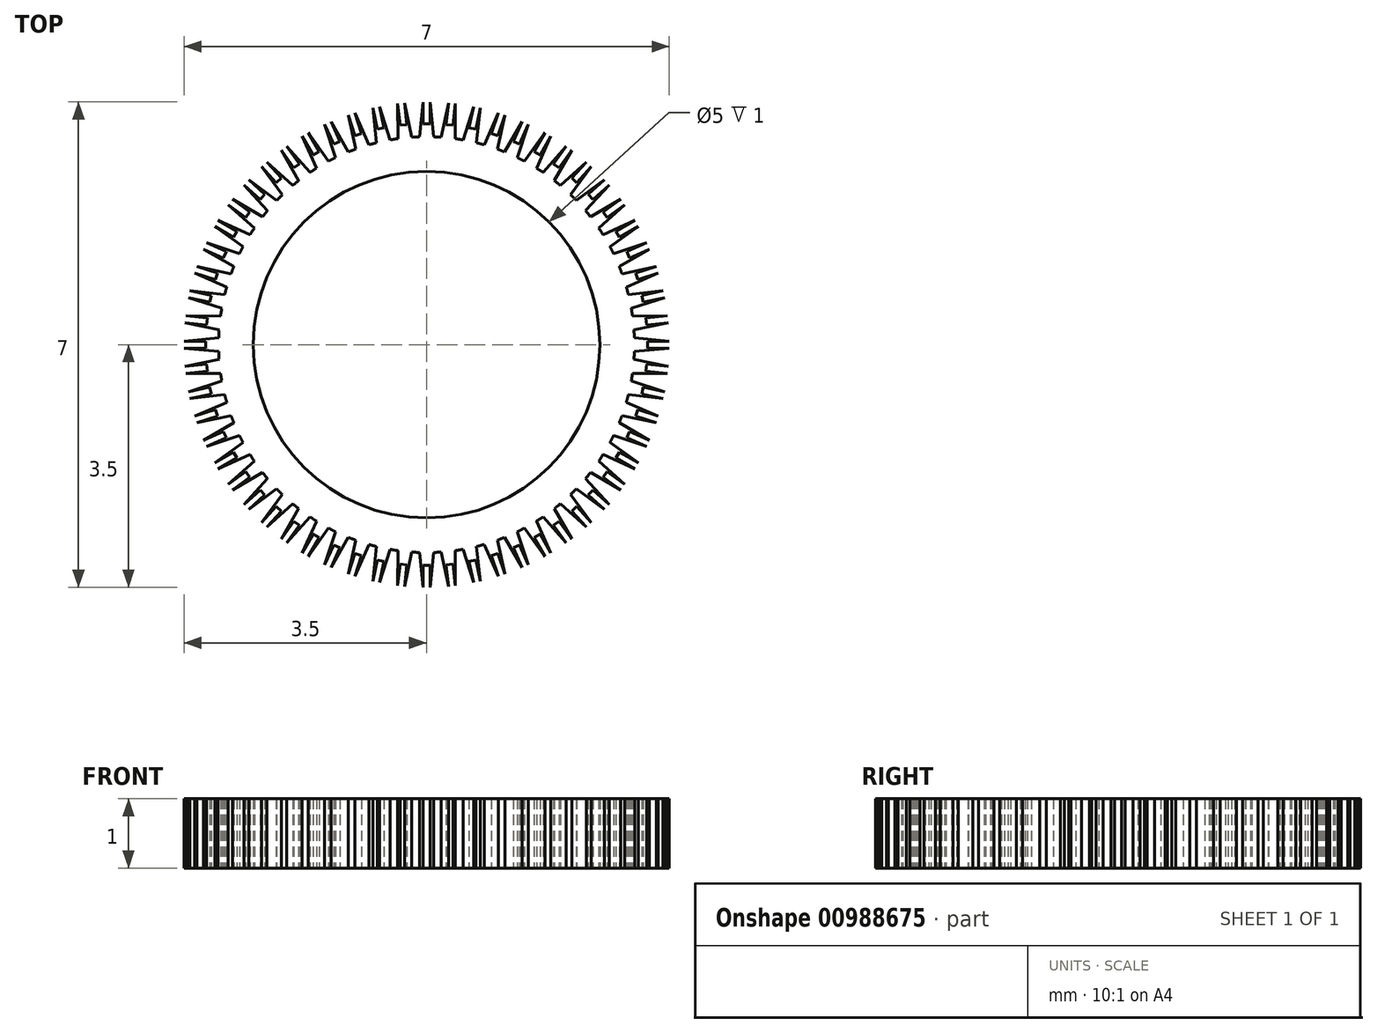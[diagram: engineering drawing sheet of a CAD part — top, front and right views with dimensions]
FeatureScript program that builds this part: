
annotation { "Feature Type Name" : "Feature", "Feature Type Description" : "" }
export const myFeature = defineFeature(function(context is Context, id is Id, definition is map)
    precondition{}
    {
        {
            var Q0;
            Q0=qCreatedBy(makeId("Top.planeOp"),FACE);
            var sketch = newSketch(context, id + "F0", { "sketchPlane" : qUnion([Q0])});
            skCircle(sketch, "E0", {"center": v(0, 0) * mm, "radius": 3 * mm});
            skCircle(sketch, "E1", {"center": v(0, 0) * mm, "radius": 3.5 * mm});
            skLineSegment(sketch, "E2", {"start": v(0, 0) * mm, "end": v(-3.5, 0) * mm});
            skLineSegment(sketch, "E3", {"start": v(0, 0) * mm, "end": v(0, 0.1) * mm});
            skLineSegment(sketch, "E4", {"start": v(0, 0) * mm, "end": v(0, -0.1) * mm});
            skLineSegment(sketch, "E5", {"start": v(0, -0.1) * mm, "end": v(-3, -0.1) * mm});
            skLineSegment(sketch, "E6", {"start": v(0, 0.1) * mm, "end": v(-3, 0.1) * mm});
            skLineSegment(sketch, "E7", {"start": v(-3.19, 0) * mm, "end": v(-3.5, 0) * mm});
            skLineSegment(sketch, "E8", {"start": v(-3.19, 0) * mm, "end": v(-3.19, 0.05) * mm});
            skLineSegment(sketch, "E9", {"start": v(-3.19, 0) * mm, "end": v(-3.19, -0.05) * mm});
            skLineSegment(sketch, "E10", {"start": v(-3.5, -0.05) * mm, "end": v(-3.19, -0.05) * mm});
            skLineSegment(sketch, "E11", {"start": v(-3.5, 0.05) * mm, "end": v(-3.19, 0.05) * mm});
            skLineSegment(sketch, "E12", {"start": v(-3, -0.1) * mm, "end": v(-3.5, -0.05) * mm});
            skLineSegment(sketch, "E13", {"start": v(-3, 0.1) * mm, "end": v(-3.5, 0.05) * mm});
            skCircle(sketch, "E14", {"center": v(0, 0) * mm, "radius": 2.5 * mm});
            skSolve(sketch);
        }
        {
            var Q0;
            {var subQ0=sQuery(id+"F0.wireOp",EDGE,"E5");var subQ5=sQuery(id+"F0.wireOp",EDGE,"E14");var subQ6=makeQuery(id+"F0.imprint","INTERSECT",VERTEX,{"derivedFrom":[subQ0,subQ5]});Q0=makeQuery(id+"F0.imprint","IMPRINT",FACE,{"disambiguationData":[TD([[makeQuery(id+"F0.imprint","IMPRINT",EDGE,{"disambiguationData":[TD([[subQ6,-1.0]])],"derivedFrom":subQ5}),-1.0]])]});}
            var Q1;
            {var subQ1=sQuery(id+"F0.wireOp",EDGE,"E0");var subQ3=sQuery(id+"F0.wireOp",EDGE,"E2");var subQ4=makeQuery(id+"F0.imprint","INTERSECT",VERTEX,{"derivedFrom":[subQ1,subQ3]});Q1=makeQuery(id+"F0.imprint","IMPRINT",FACE,{"disambiguationData":[TD([[makeQuery(id+"F0.imprint","IMPRINT",EDGE,{"disambiguationData":[TD([[subQ4,1.0]])],"derivedFrom":subQ3}),1.0]])]});}
            var Q2;
            {var subQ1=sQuery(id+"F0.wireOp",EDGE,"E0");var subQ3=sQuery(id+"F0.wireOp",EDGE,"E2");var subQ4=makeQuery(id+"F0.imprint","INTERSECT",VERTEX,{"derivedFrom":[subQ1,subQ3]});Q2=makeQuery(id+"F0.imprint","IMPRINT",FACE,{"disambiguationData":[TD([[makeQuery(id+"F0.imprint","IMPRINT",EDGE,{"disambiguationData":[TD([[subQ4,1.0]])],"derivedFrom":subQ3}),-1.0]])]});}
            var Q3;
            {var subQ0=sQuery(id+"F0.wireOp",EDGE,"E7");Q3=makeQuery(id+"F0.imprint","IMPRINT",FACE,{"disambiguationData":[TD([[makeQuery(id+"F0.imprint","IMPRINT",EDGE,{"derivedFrom":subQ0}),1.0]])]});}
            var Q4;
            {var subQ0=sQuery(id+"F0.wireOp",EDGE,"E7");Q4=makeQuery(id+"F0.imprint","IMPRINT",FACE,{"disambiguationData":[TD([[makeQuery(id+"F0.imprint","IMPRINT",EDGE,{"derivedFrom":subQ0}),-1.0]])]});}
            var Q5;
            {var subQ0=sQuery(id+"F0.wireOp",EDGE,"E8");Q5=makeQuery(id+"F0.imprint","IMPRINT",FACE,{"disambiguationData":[TD([[makeQuery(id+"F0.imprint","IMPRINT",EDGE,{"derivedFrom":subQ0}),-1.0]])]});}
            var Q6;
            {var subQ0=sQuery(id+"F0.wireOp",EDGE,"E9");Q6=makeQuery(id+"F0.imprint","IMPRINT",FACE,{"disambiguationData":[TD([[makeQuery(id+"F0.imprint","IMPRINT",EDGE,{"derivedFrom":subQ0}),1.0]])]});}
            extrude(context, id + "F1", {"entities" : qUnion([Q0, Q1, Q2, Q3, Q4, Q5, Q6]), "depth" : 1 * mm, "offsetDistance" : 25 * mm});
        }
        {
            var Q0;
            Q0=makeQuery(id+"F1.opExtrude","SWEPT_BODY",BODY,{"disambiguationData":[OSD([sQuery(id+"F0.wireOp",EDGE,"E0"),sQuery(id+"F0.wireOp",EDGE,"E1"),sQuery(id+"F0.wireOp",EDGE,"E12"),sQuery(id+"F0.wireOp",EDGE,"E13"),sQuery(id+"F0.wireOp",EDGE,"E14")])]});
            var Q1;
            Q1=makeQuery(id+"F1.opExtrude","SWEPT_FACE",FACE,{"disambiguationData":[OSD([sQuery(id+"F0.wireOp",EDGE,"E0")])]});
            circularPattern(context, id + "F2", {"operationType" : NewBodyOperationType.ADD, "entities" : qUnion([Q0]), "axis" : qUnion([Q1]), "angle" : 360 * degree, "instanceCount" : 60, "equalSpace" : true});
        }
    });
